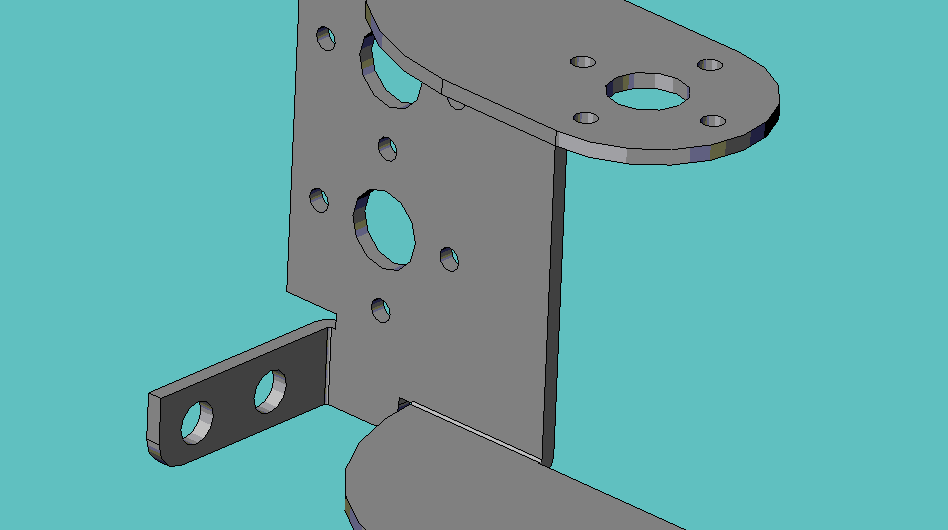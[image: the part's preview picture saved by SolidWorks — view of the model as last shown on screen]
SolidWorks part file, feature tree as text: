
SOLIDWORKS PART (.sldprt)
format: sldprt  version: not decoded by parser v0  size: 240,128 bytes
history: native  units: mm
features: sketch x6, extrude x3, cut_extrude x3, fillet x3, material x1 (+12 scaffold rows collapsed)
feature tree (28):
  scaffold x12  (default folders/planes/origin — collapsed)
  material  "Material <not specified>"
  sketch  "Sketch1"  dims[D1=68.2752mm]
  extrude  "Extrude1"  Depth=1.5875mm
  extrude  "Extrude2"  [1 undecoded]
  sketch  "Sketch1<3>"  dims[D1=24.2062mm]
  extrude  "Extrude3"  [1 undecoded]
  sketch  "Sketch1<4>"  dims[D1=26.5938mm]
  sketch  "Sketch2"  dims[D1=26.5938mm]
  cut_extrude  "Cut-Extrude1"  Depth=26.5938mm
  cut_extrude  "Cut-Extrude2"  [1 undecoded]
  sketch  "Sketch2<3>"  dims[D1=26.5938mm]
  sketch  "Sketch3"  dims[D1=19.1262mm]
  cut_extrude  "Cut-Extrude3"  [1 undecoded]
  fillet  "Fillet1"  Radius=3.175mm
  fillet  "Fillet2"  Radius=1.778mm
  fillet  "Fillet3"  Radius=0.254mm
decode coverage: 11 of 15 modeling features carry decoded parameters
note: 4 parameter values undecoded
summary: no parameter record found for 4 features
note: suppression state not decoded; provenance and decode notes live in map.json
